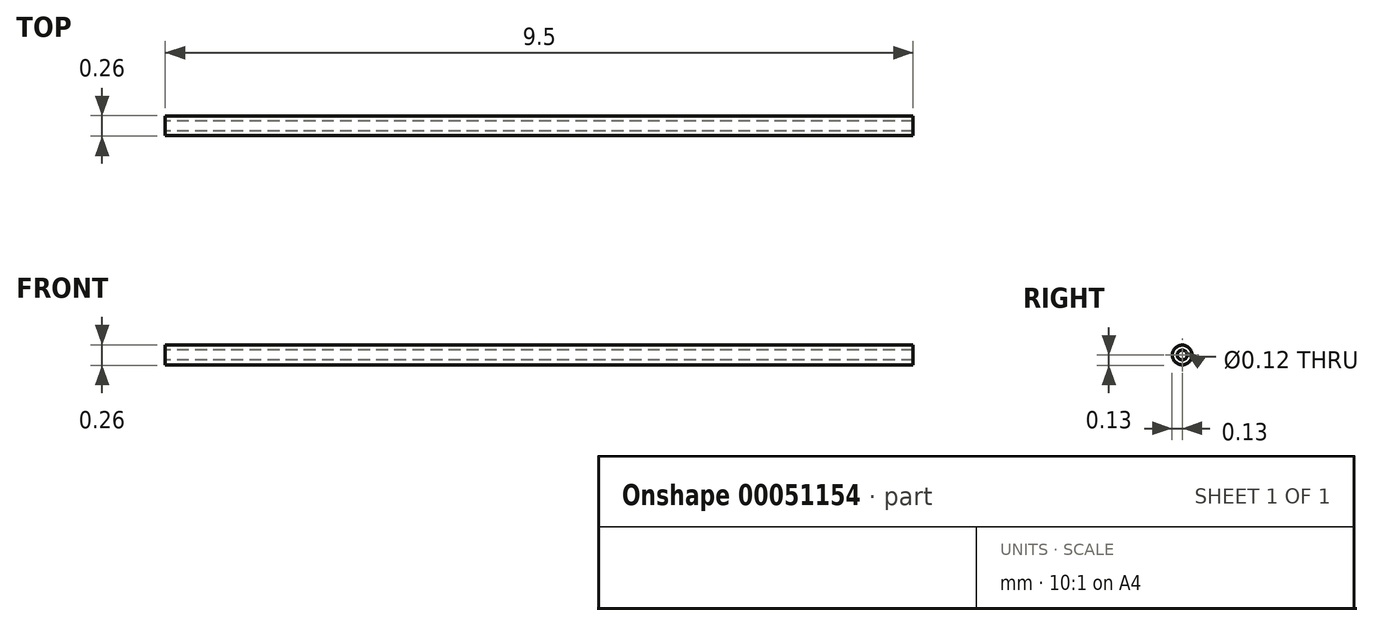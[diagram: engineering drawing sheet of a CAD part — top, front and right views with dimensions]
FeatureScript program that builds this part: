
annotation { "Feature Type Name" : "Feature", "Feature Type Description" : "" }
export const myFeature = defineFeature(function(context is Context, id is Id, definition is map)
    precondition{}
    {
        {
            var Q0;
            Q0=qCreatedBy(makeId("Right.planeOp"),FACE);
            var sketch = newSketch(context, id + "F0", { "sketchPlane" : qUnion([Q0])});
            skCircle(sketch, "E0", {"center": v(0, 0) * mm, "radius": 0.06 * mm});
            skCircle(sketch, "E1", {"center": v(0, 0) * mm, "radius": 0.12 * mm});
            skSolve(sketch);
        }
        {
            var Q0;
            Q0 = qSketchRegion(id + "F0", true);
            extrude(context, id + "F1", {"entities" : qUnion([Q0]), "depth" : 9.5 * mm});
        }
    });
